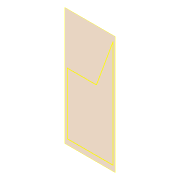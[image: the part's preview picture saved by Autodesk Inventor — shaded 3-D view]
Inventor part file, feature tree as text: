
AUTODESK INVENTOR PART (.ipt)
format: ipt  version: 2022 (Build 260153000, 153)  size: 64,000 bytes
history: native  units: in
note: dims shown in document units (in); Inventor stores cm internally (conversion verified against a paired STEP export)
features: other x2, plane x1, sketch x1, reference x1
ambient origin geometry x8: Origin, YZ Plane, XZ Plane, XY Plane, X Axis, Y Axis, Z Axis, Center Point
feature tree (5):
  plane  "Work Plane1"
  sketch  "Sketch1"
  reference  "Reference1"
  other  "Assembly2"
  other  "Modelo base:1"
